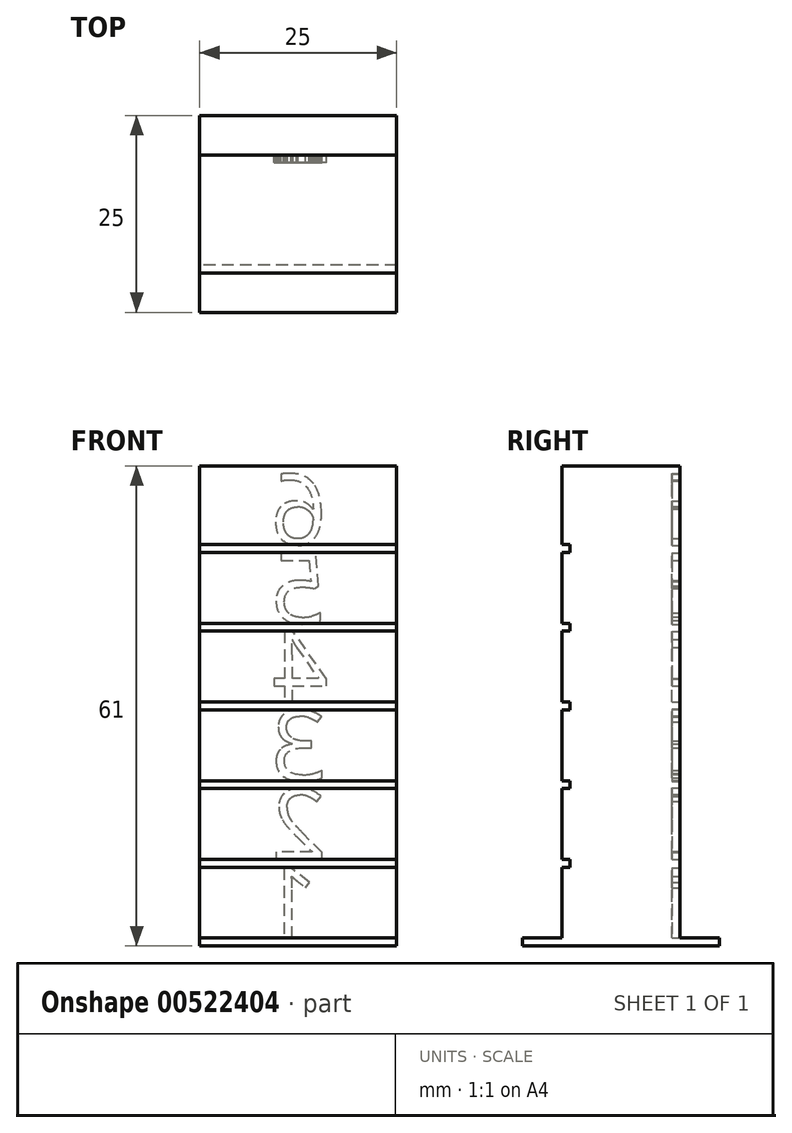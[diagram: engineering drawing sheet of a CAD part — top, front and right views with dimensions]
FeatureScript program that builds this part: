
annotation { "Feature Type Name" : "Feature", "Feature Type Description" : "" }
export const myFeature = defineFeature(function(context is Context, id is Id, definition is map)
    precondition{}
    {
        {
            var Q0;
            Q0=qCreatedBy(makeId("Top.planeOp"),FACE);
            var sketch = newSketch(context, id + "F0", { "sketchPlane" : qUnion([Q0])});
            skLineSegment(sketch, "E0.bottom", {"start": v(12.5, 12.5) * mm, "end": v(-12.5, 12.5) * mm});
            skLineSegment(sketch, "E0.top", {"start": v(12.5, -12.5) * mm, "end": v(-12.5, -12.5) * mm});
            skLineSegment(sketch, "E0.left", {"start": v(12.5, 12.5) * mm, "end": v(12.5, -12.5) * mm});
            skLineSegment(sketch, "E0.right", {"start": v(-12.5, 12.5) * mm, "end": v(-12.5, -12.5) * mm});
            skPoint(sketch, "E0.middle", {"position": v(0, 0) * mm});
            skSolve(sketch);
        }
        {
            var Q0;
            Q0 = qSketchRegion(id + "F0", true);
            extrude(context, id + "F1", {"entities" : qUnion([Q0]), "depth" : 1 * mm, "offsetDistance" : 25 * mm});
        }
        {
            var Q0;
            Q0=makeQuery(id+"F1.opExtrude","CAP_FACE",FACE,{"disambiguationData":[OSD([sQuery(id+"F0.wireOp",EDGE,"E0.bottom"),sQuery(id+"F0.wireOp",EDGE,"E0.top"),sQuery(id+"F0.wireOp",EDGE,"E0.left"),sQuery(id+"F0.wireOp",EDGE,"E0.right")])],"isStart":false});
            var sketch = newSketch(context, id + "F2", { "sketchPlane" : qUnion([Q0])});
            skLineSegment(sketch, "E1.bottom", {"start": v(12.5, 7.5) * mm, "end": v(-12.5, 7.5) * mm});
            skLineSegment(sketch, "E1.top", {"start": v(12.5, -7.5) * mm, "end": v(-12.5, -7.5) * mm});
            skLineSegment(sketch, "E1.left", {"start": v(12.5, 7.5) * mm, "end": v(12.5, -7.5) * mm});
            skLineSegment(sketch, "E1.right", {"start": v(-12.5, 7.5) * mm, "end": v(-12.5, -7.5) * mm});
            skPoint(sketch, "E1.middle", {"position": v(0, 0) * mm});
            skSolve(sketch);
        }
        {
            var Q0;
            Q0 = qSketchRegion(id + "F2", true);
            extrude(context, id + "F3", {"entities" : qUnion([Q0]), "operationType" : NewBodyOperationType.ADD, "depth" : 60 * mm, "offsetDistance" : 25 * mm});
        }
        {
            var Q0;
            Q0=makeQuery(id+"F3.boolean.opBoolean","MERGE",FACE,{"derivedFrom":[makeQuery(id+"F1.opExtrude","SWEPT_FACE",FACE,{"disambiguationData":[OSD([sQuery(id+"F0.wireOp",EDGE,"E0.right")])]}),makeQuery(id+"F3.opExtrude","SWEPT_FACE",FACE,{"disambiguationData":[OSD([sQuery(id+"F2.wireOp",EDGE,"E1.right")])]})]});
            var sketch = newSketch(context, id + "F4", { "sketchPlane" : qUnion([Q0])});
            skLineSegment(sketch, "E2", {"start": v(7.5, 1) * mm, "end": v(7.5, 10) * mm});
            skLineSegment(sketch, "E3", {"start": v(7.5, 10) * mm, "end": v(6.5, 10) * mm});
            skLineSegment(sketch, "E4", {"start": v(6.5, 10) * mm, "end": v(6.5, 11) * mm});
            skLineSegment(sketch, "E5", {"start": v(6.5, 11) * mm, "end": v(7.5, 11) * mm});
            skLineSegment(sketch, "E6", {"start": v(7.5, 11) * mm, "end": v(7.5, 20) * mm});
            skLineSegment(sketch, "E7", {"start": v(7.5, 20) * mm, "end": v(6.5, 20) * mm});
            skLineSegment(sketch, "E8", {"start": v(6.5, 20) * mm, "end": v(6.5, 21) * mm});
            skLineSegment(sketch, "E9", {"start": v(6.5, 21) * mm, "end": v(7.5, 21) * mm});
            skLineSegment(sketch, "E10", {"start": v(7.5, 21) * mm, "end": v(7.5, 30) * mm});
            skLineSegment(sketch, "E11", {"start": v(7.5, 30) * mm, "end": v(6.5, 30) * mm});
            skLineSegment(sketch, "E12", {"start": v(6.5, 30) * mm, "end": v(6.5, 31) * mm});
            skLineSegment(sketch, "E13", {"start": v(6.5, 31) * mm, "end": v(7.5, 31) * mm});
            skLineSegment(sketch, "E14", {"start": v(7.5, 31) * mm, "end": v(7.5, 40) * mm});
            skLineSegment(sketch, "E15", {"start": v(7.5, 40) * mm, "end": v(6.5, 40) * mm});
            skLineSegment(sketch, "E16", {"start": v(6.5, 40) * mm, "end": v(6.5, 41) * mm});
            skLineSegment(sketch, "E17", {"start": v(6.5, 41) * mm, "end": v(7.5, 41) * mm});
            skLineSegment(sketch, "E18", {"start": v(7.5, 41) * mm, "end": v(7.5, 50) * mm});
            skLineSegment(sketch, "E19", {"start": v(7.5, 50) * mm, "end": v(6.5, 50) * mm});
            skLineSegment(sketch, "E20", {"start": v(6.5, 50) * mm, "end": v(6.5, 51) * mm});
            skLineSegment(sketch, "E21", {"start": v(6.5, 51) * mm, "end": v(7.5, 51) * mm});
            skLineSegment(sketch, "E22", {"start": v(7.5, 51) * mm, "end": v(7.5, 10) * mm});
            skSolve(sketch);
        }
        {
            var Q0;
            Q0 = qSketchRegion(id + "F4", true);
            extrude(context, id + "F5", {"entities" : qUnion([Q0]), "operationType" : NewBodyOperationType.REMOVE, "endBound" : BoundingType.THROUGH_ALL, "oppositeDirection" : true, "depth" : 25 * mm, "offsetDistance" : 25 * mm});
        }
        {
            var Q0;
            Q0=makeQuery(id+"F3.opExtrude","SWEPT_FACE",FACE,{"disambiguationData":[OSD([sQuery(id+"F2.wireOp",EDGE,"E1.bottom")])]});
            var sketch = newSketch(context, id + "F6", { "sketchPlane" : qUnion([Q0])});
            skText(sketch, "E23", { "text": "1", "fontName": "OpenSans-Regular.ttf"});
            skText(sketch, "E24", { "text": "2", "fontName": "OpenSans-Regular.ttf"});
            skText(sketch, "E25", { "text": "4", "fontName": "OpenSans-Regular.ttf"});
            skText(sketch, "E26", { "text": "5", "fontName": "OpenSans-Regular.ttf"});
            skPoint(sketch, "E26.firstSnap0", {"position": v(1.9, 50) * mm});
            skText(sketch, "E27", { "text": "6", "fontName": "OpenSans-Regular.ttf"});
            skText(sketch, "E28", { "text": "3", "fontName": "OpenSans-Regular.ttf"});
            const initialGuessF6  = {"E23": [-0.00259, 0.001, 1, 0, 0.009], "E24": [-0.00364, 0.011, 1, 0, 0.009], "E25": [-0.00385, 0.031, 1, 0, 0.009], "E26": [-0.00362, 0.041, 1, 0, 0.009], "E27": [-0.00367, 0.051, 1, 0, 0.009], "E28": [-0.00361, 0.021, 1, 0, 0.009]};
            skSetInitialGuess(sketch, initialGuessF6);
            skSolve(sketch);
        }
        {
            var Q0;
            Q0 = qSketchRegion(id + "F6", true);
            extrude(context, id + "F7", {"entities" : qUnion([Q0]), "operationType" : NewBodyOperationType.REMOVE, "oppositeDirection" : true, "depth" : 1 * mm, "offsetDistance" : 25 * mm});
        }
    });
